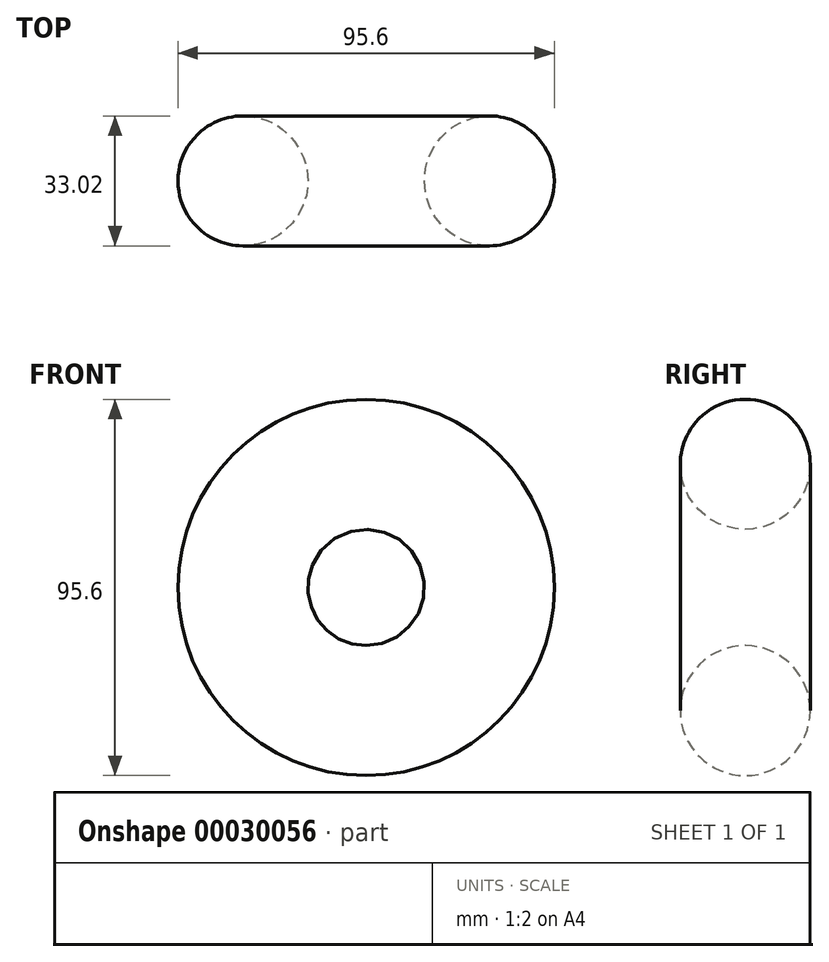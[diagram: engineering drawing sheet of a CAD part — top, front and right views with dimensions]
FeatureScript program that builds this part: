
annotation { "Feature Type Name" : "Feature", "Feature Type Description" : "" }
export const myFeature = defineFeature(function(context is Context, id is Id, definition is map)
    precondition{}
    {
        {
            var Q0;
            Q0=qCreatedBy(makeId("Right.planeOp"),FACE);
            var sketch = newSketch(context, id + "F0", { "sketchPlane" : qUnion([Q0])});
            skCircle(sketch, "E0", {"center": v(0, 0) * mm, "radius": 16.51 * mm});
            skLineSegment(sketch, "E1", {"start": v(-39.72, -31.29) * mm, "end": v(49.18, -31.29) * mm});
            skSolve(sketch);
        }
        {
            var Q0;
            Q0=makeQuery(id+"F0.imprint","IMPRINT",FACE,{"disambiguationData":[TD([[makeQuery(id+"F0.imprint","IMPRINT",EDGE,{"derivedFrom":sQuery(id+"F0.wireOp",EDGE,"E0")}),1.0]])]});
            var Q1;
            Q1=sQuery(id+"F0.wireOp",EDGE,"E1");
            revolve(context, id + "F1", {"entities" : qUnion([Q0]), "axis" : qUnion([Q1]), "revolveType" : RevolveType.FULL});
        }
    });
